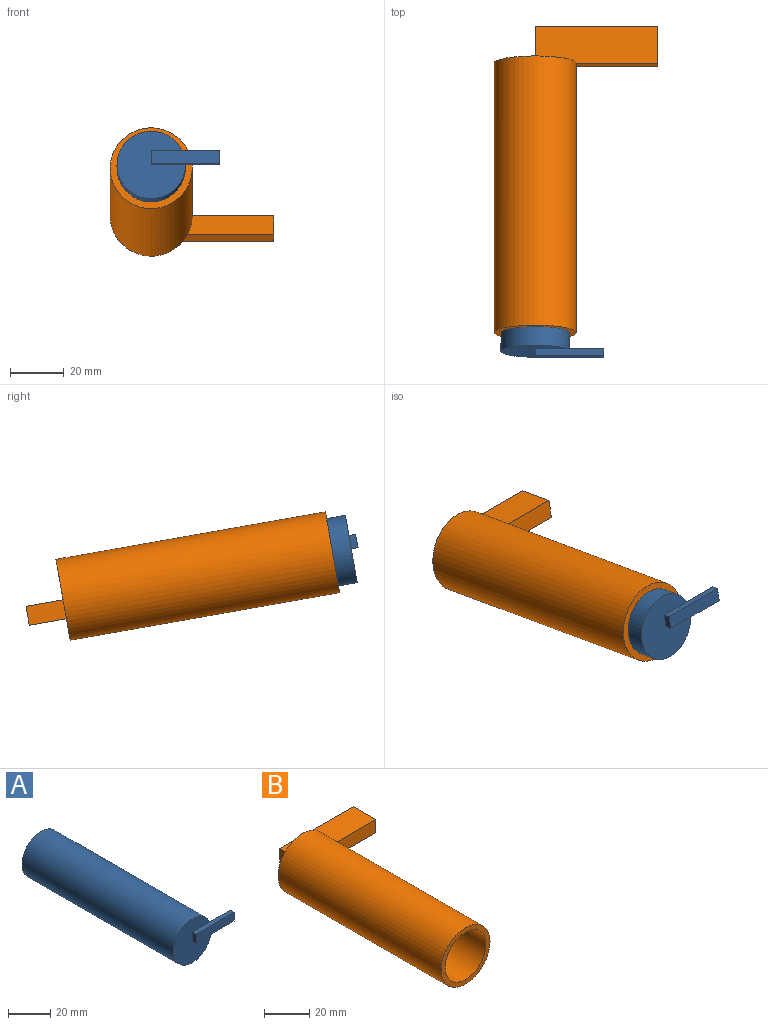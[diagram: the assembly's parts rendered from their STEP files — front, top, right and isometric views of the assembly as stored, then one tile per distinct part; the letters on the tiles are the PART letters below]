
ASSEMBLY  parts=2 mates=1
PART A: 9 faces, bbox 38.1x104.1x25.4 mm
  f0: plane 25.4x25.4mm, normal (0,-1,0), area 444mm2, adj f1,f4,f5,f6
  f1: cylinder r=12.7mm len=101.6mm, axis (0,1,0), area 8107.3mm2, adj f0,f2,f3
  f2: plane 25.4x25.4mm, normal (0,1,0), area 506.7mm2, adj f1
  f3: plane 13.76x5.08mm, normal (0,1,0), area 66.3mm2, adj f1,f4,f6,f7
  f4: plane 25.4x2.54mm, normal (0,0,1), area 64.5mm2, adj f0,f3,f5,f7,f8
  f5: plane 5.08x2.54mm, normal (-1,0,0), area 12.9mm2, adj f0,f4,f6,f8
  f6: plane 25.4x2.54mm, normal (0,0,-1), area 64.5mm2, adj f0,f3,f5,f7,f8
  f7: plane 5.08x2.54mm, normal (1,0,0), area 12.9mm2, adj f3,f4,f6,f8
  f8: plane 25.4x5.08mm, normal (0,-1,0), area 129mm2, adj f4,f5,f6,f7
PART B: 11 faces, bbox 60.8x115.6x30.5 mm
  f0: cylinder r=15.24mm len=101.6mm, axis (0,1,0), area 9728.8mm2, adj f1,f2,f9
  f1: plane 30.48x30.48mm, normal (0,-1,0), area 223mm2, adj f0,f3
  f2: plane 30.48x30.48mm, normal (0,1,0), area 624.7mm2, adj f0,f5,f6,f7
  f3: cylinder r=12.7mm len=99.06mm, axis (0,1,0), area 7904.6mm2, adj f1,f4
  f4: plane 25.4x25.4mm, normal (0,-1,0), area 506.7mm2, adj f3
  f5: plane 45.53x14mm, normal (0,0,-1), area 637.3mm2, adj f2,f6,f8,f9,f10
  f6: plane 14x7.16mm, normal (-1,0,0), area 100.2mm2, adj f2,f5,f7,f10
  f7: plane 45.53x14mm, normal (0,0,1), area 637.3mm2, adj f2,f6,f8,f9,f10
  f8: plane 14x7.16mm, normal (1,0,0), area 100.2mm2, adj f5,f7,f9,f10
  f9: plane 32.08x7.16mm, normal (0,-1,0), area 221.1mm2, adj f0,f5,f7,f8
  f10: plane 45.53x7.16mm, normal (0,1,0), area 326.1mm2, adj f5,f6,f7,f8
PLACE A rot(axis=(-1,0,0),10deg) t=(31.47,39.42,-80.7)mm
PLACE B rot(axis=(-1,0,0),10deg) t=(31.47,46.4,-81.93)mm
MATE cylindrical B.f0 <-> A.f1  axis (0,0.98,-0.17) through (31.47,-4.88,-72.88)mm
